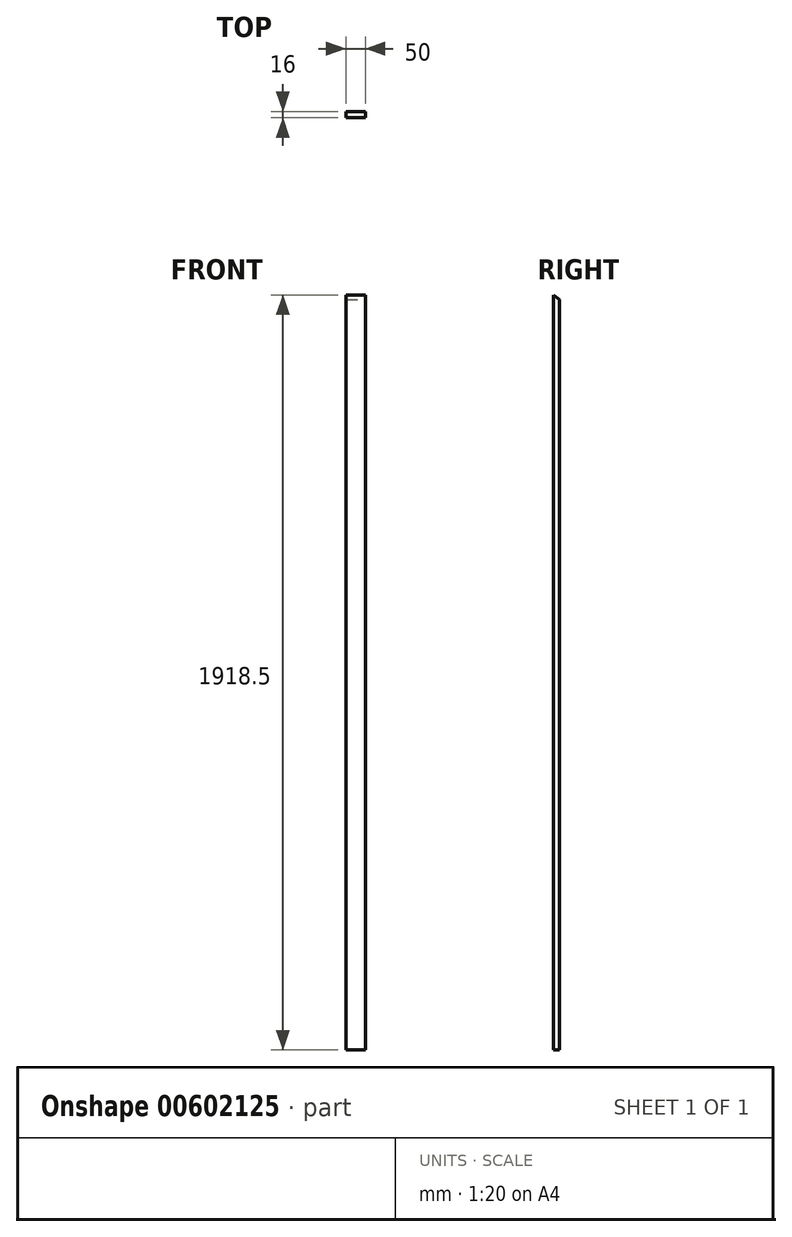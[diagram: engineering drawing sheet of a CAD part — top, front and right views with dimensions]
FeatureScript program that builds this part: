
annotation { "Feature Type Name" : "Feature", "Feature Type Description" : "" }
export const myFeature = defineFeature(function(context is Context, id is Id, definition is map)
    precondition{}
    {
        {
            var Q0;
            Q0=qCreatedBy(makeId("Top.planeOp"),FACE);
            var sketch = newSketch(context, id + "F0", { "sketchPlane" : qUnion([Q0])});
            skLineSegment(sketch, "E0.bottom", {"start": v(0, 0) * mm, "end": v(50, 0) * mm});
            skLineSegment(sketch, "E0.top", {"start": v(0, -16) * mm, "end": v(50, -16) * mm});
            skLineSegment(sketch, "E0.left", {"start": v(0, 0) * mm, "end": v(0, -16) * mm});
            skLineSegment(sketch, "E0.right", {"start": v(50, 0) * mm, "end": v(50, -16) * mm});
            skSolve(sketch);
        }
        {
            var Q0;
            Q0 = qSketchRegion(id + "F0", true);
            extrude(context, id + "F1", {"entities" : qUnion([Q0]), "depth" : (1915 + 3.5) * mm, "offsetDistance" : 25 * mm});
        }
        {
            var Q0;
            Q0=makeQuery(id+"F1.opExtrude","SWEPT_FACE",FACE,{"disambiguationData":[OSD([sQuery(id+"F0.wireOp",EDGE,"E0.right")])]});
            var sketch = newSketch(context, id + "F2", { "sketchPlane" : qUnion([Q0])});
            skLineSegment(sketch, "E1", {"start": v(-16, 1918.5) * mm, "end": v(0, 1906.44) * mm});
            skLineSegment(sketch, "E2", {"start": v(0, 1906.44) * mm, "end": v(0, 1918.5) * mm});
            skLineSegment(sketch, "E3", {"start": v(0, 1918.5) * mm, "end": v(-16, 1918.5) * mm});
            skSolve(sketch);
        }
        {
            var Q0;
            Q0 = qSketchRegion(id + "F2", true);
            extrude(context, id + "F3", {"entities" : qUnion([Q0]), "operationType" : NewBodyOperationType.REMOVE, "endBound" : BoundingType.UP_TO_NEXT, "oppositeDirection" : true, "depth" : 25 * mm, "offsetDistance" : 25 * mm});
        }
    });
